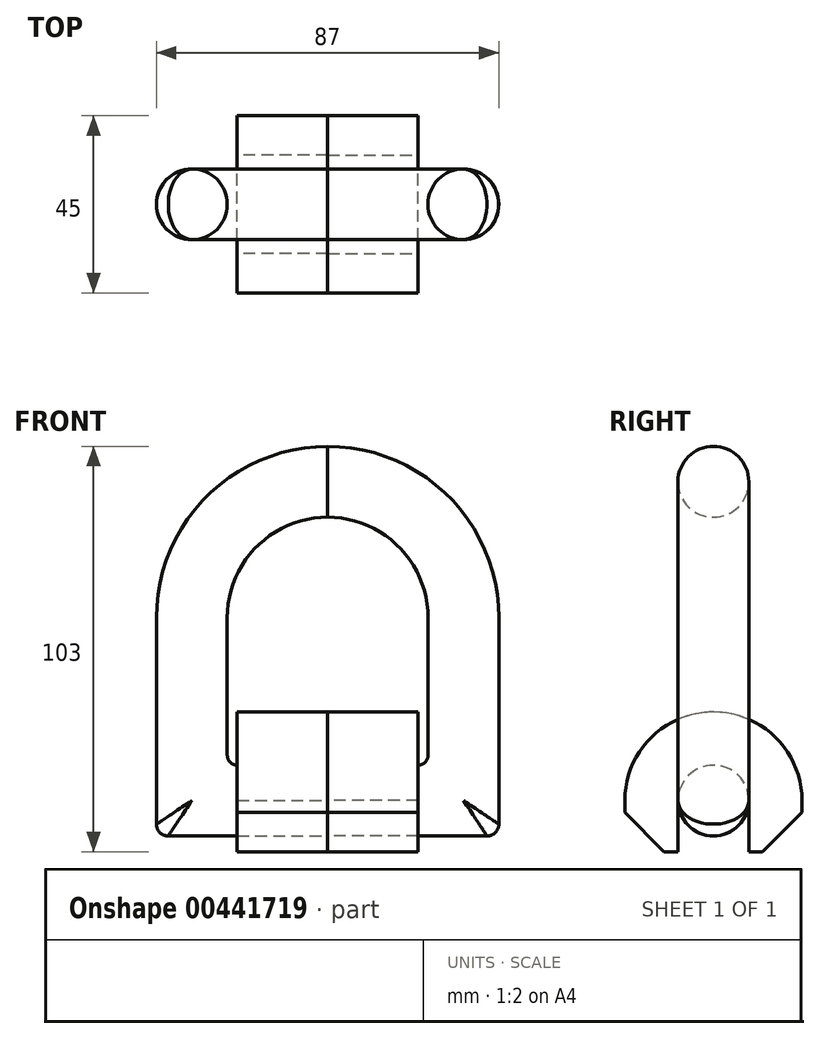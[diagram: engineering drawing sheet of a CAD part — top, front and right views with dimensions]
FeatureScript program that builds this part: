
annotation { "Feature Type Name" : "Feature", "Feature Type Description" : "" }
export const myFeature = defineFeature(function(context is Context, id is Id, definition is map)
    precondition{}
    {
        {
            var Q0;
            Q0=qCreatedBy(makeId("Front.planeOp"),FACE);
            var sketch = newSketch(context, id + "F0", { "sketchPlane" : qUnion([Q0])});
            skLineSegment(sketch, "E0.bottom", {"start": v(0, 0) * mm, "end": v(-23, 0) * mm});
            skLineSegment(sketch, "E0.top", {"start": v(0, 63) * mm, "end": v(0, 63) * mm});
            skLineSegment(sketch, "E0.left", {"start": v(0, 0) * mm, "end": v(0, 63) * mm, "construction": true});
            skLineSegment(sketch, "E0.right", {"start": v(-25.5, 2.5) * mm, "end": v(-25.5, 37.5) * mm});
            skPoint(sketch, "E1.visualSharp", {"position": v(-25.5, 63) * mm});
            skArc(sketch, "E1.filletArc", {"start": v(0, 63) * mm, "mid": v(-18.03, 55.53) * mm, "end": v(-25.5, 37.5) * mm});
            skPoint(sketch, "E2.visualSharp", {"position": v(-25.5, 0) * mm});
            skArc(sketch, "E2.filletArc", {"start": v(-25.5, 2.5) * mm, "mid": v(-24.77, 0.73) * mm, "end": v(-23, 0) * mm});
            skArc(sketch, "E3.0", {"start": v(0, 81) * mm, "mid": v(-30.76, 68.26) * mm, "end": v(-43.5, 37.5) * mm});
            skLineSegment(sketch, "E3.1", {"start": v(-43.5, -15) * mm, "end": v(-43.5, 37.5) * mm});
            skLineSegment(sketch, "E3.3", {"start": v(0, -18) * mm, "end": v(-40.5, -18) * mm});
            skArc(sketch, "E4", {"start": v(-43.5, -15) * mm, "mid": v(-42.62, -17.12) * mm, "end": v(-40.5, -18) * mm});
            skLineSegment(sketch, "E5", {"start": v(0, -18) * mm, "end": v(0, 0) * mm});
            skLineSegment(sketch, "E6", {"start": v(0, 63) * mm, "end": v(0, 81) * mm});
            skSolve(sketch);
        }
        {
            var Q0;
            Q0=makeQuery(id+"F0.imprint","IMPRINT",FACE,{"disambiguationData":[TD([[makeQuery(id+"F0.imprint","IMPRINT",EDGE,{"derivedFrom":sQuery(id+"F0.wireOp",EDGE,"E0.bottom")}),1.0]])]});
            extrude(context, id + "F1", {"entities" : qUnion([Q0]), "endBound" : BoundingType.SYMMETRIC, "depth" : 18 * mm});
        }
        {
            var Q0;
            Q0=makeQuery(id+"F1.opExtrude","CAP_EDGE",EDGE,{"disambiguationData":[OSD([sQuery(id+"F0.wireOp",EDGE,"E3.0")])],"isStart":false});
            var Q1;
            Q1=makeQuery(id+"F1.opExtrude","CAP_EDGE",EDGE,{"disambiguationData":[OSD([sQuery(id+"F0.wireOp",EDGE,"E0.bottom")])],"isStart":false});
            var Q2;
            Q2=makeQuery(id+"F1.opExtrude","CAP_EDGE",EDGE,{"disambiguationData":[OSD([sQuery(id+"F0.wireOp",EDGE,"E0.bottom")])],"isStart":true});
            var Q3;
            Q3=makeQuery(id+"F1.opExtrude","CAP_EDGE",EDGE,{"disambiguationData":[OSD([sQuery(id+"F0.wireOp",EDGE,"E3.3")])],"isStart":true});
            fillet(context, id + "F2", {"entities" : qUnion([Q0, Q1, Q2, Q3]), "radius" : 9 * mm, "tangentPropagation" : true, "allowEdgeOverflow" : false});
        }
        {
            var Q0;
            Q0=qCreatedBy(makeId("Right.planeOp"),FACE);
            var sketch = newSketch(context, id + "F3", { "sketchPlane" : qUnion([Q0])});
            skArc(sketch, "E7.0", {"start": v(0, 0) * mm, "mid": v(-6.36, -2.64) * mm, "end": v(-9, -9) * mm});
            skArc(sketch, "E8", {"start": v(0, 13.5) * mm, "mid": v(-15.9, 6.9) * mm, "end": v(-22.5, -9) * mm});
            skLineSegment(sketch, "E9", {"start": v(-9, -9) * mm, "end": v(-9, -22) * mm});
            skLineSegment(sketch, "E10", {"start": v(-9, -22) * mm, "end": v(-22.5, -22) * mm});
            skLineSegment(sketch, "E11", {"start": v(-22.5, -22) * mm, "end": v(-22.5, -9) * mm});
            skLineSegment(sketch, "E12", {"start": v(0, 0) * mm, "end": v(0, 13.5) * mm});
            skSolve(sketch);
        }
        {
            var Q0;
            Q0=makeQuery(id+"F3.imprint","IMPRINT",FACE,{"disambiguationData":[TD([[makeQuery(id+"F3.imprint","IMPRINT",EDGE,{"derivedFrom":sQuery(id+"F3.wireOp",EDGE,"E7.0")}),-1.0]])]});
            extrude(context, id + "F4", {"entities" : qUnion([Q0]), "oppositeDirection" : true, "depth" : 23 * mm});
        }
        {
            var Q0;
            Q0=makeQuery(id+"F4.opExtrude","SWEPT_EDGE",EDGE,{"disambiguationData":[OSD([sQuery(id+"F3.wireOp",EDGE,"E10"),sQuery(id+"F3.wireOp",EDGE,"E11")])]});
            chamfer(context, id + "F5", {"entities" : qUnion([Q0]), "width" : 10 * mm, "tangentPropagation" : true});
        }
        {
            var Q0;
            Q0=makeQuery(id+"F4.opExtrude","SWEPT_BODY",BODY,{"disambiguationData":[OSD([sQuery(id+"F3.wireOp",EDGE,"E7.0"),sQuery(id+"F3.wireOp",EDGE,"E8"),sQuery(id+"F3.wireOp",EDGE,"E9"),sQuery(id+"F3.wireOp",EDGE,"E10"),sQuery(id+"F3.wireOp",EDGE,"E11"),sQuery(id+"F3.wireOp",EDGE,"E12")])]});
            var Q1;
            Q1=makeQuery(id+"F4.opExtrude","SWEPT_FACE",FACE,{"disambiguationData":[OSD([sQuery(id+"F3.wireOp",EDGE,"E12")])]});
            mirror(context, id + "F6", {"operationType" : NewBodyOperationType.ADD, "entities" : qUnion([Q0]), "mirrorPlane" : qUnion([Q1])});
        }
        {
            var Q0;
            Q0=makeQuery(id+"F4.opExtrude","SWEPT_BODY",BODY,{"disambiguationData":[OSD([sQuery(id+"F3.wireOp",EDGE,"E7.0"),sQuery(id+"F3.wireOp",EDGE,"E8"),sQuery(id+"F3.wireOp",EDGE,"E9"),sQuery(id+"F3.wireOp",EDGE,"E10"),sQuery(id+"F3.wireOp",EDGE,"E11"),sQuery(id+"F3.wireOp",EDGE,"E12")])]});
            var Q1;
            Q1=makeQuery(id+"F1.opExtrude","SWEPT_BODY",BODY,{"disambiguationData":[OSD([sQuery(id+"F0.wireOp",EDGE,"E0.bottom"),sQuery(id+"F0.wireOp",EDGE,"E0.right"),sQuery(id+"F0.wireOp",EDGE,"E1.filletArc"),sQuery(id+"F0.wireOp",EDGE,"E2.filletArc"),sQuery(id+"F0.wireOp",EDGE,"E3.0"),sQuery(id+"F0.wireOp",EDGE,"E3.1"),sQuery(id+"F0.wireOp",EDGE,"E3.3"),sQuery(id+"F0.wireOp",EDGE,"E4"),sQuery(id+"F0.wireOp",EDGE,"E5"),sQuery(id+"F0.wireOp",EDGE,"E6")])]});
            var Q2;
            Q2=makeQuery(id+"F1.opExtrude","SWEPT_FACE",FACE,{"disambiguationData":[OSD([sQuery(id+"F0.wireOp",EDGE,"E5")])]});
            mirror(context, id + "F7", {"entities" : qUnion([Q0, Q1]), "mirrorPlane" : qUnion([Q2])});
        }
    });
